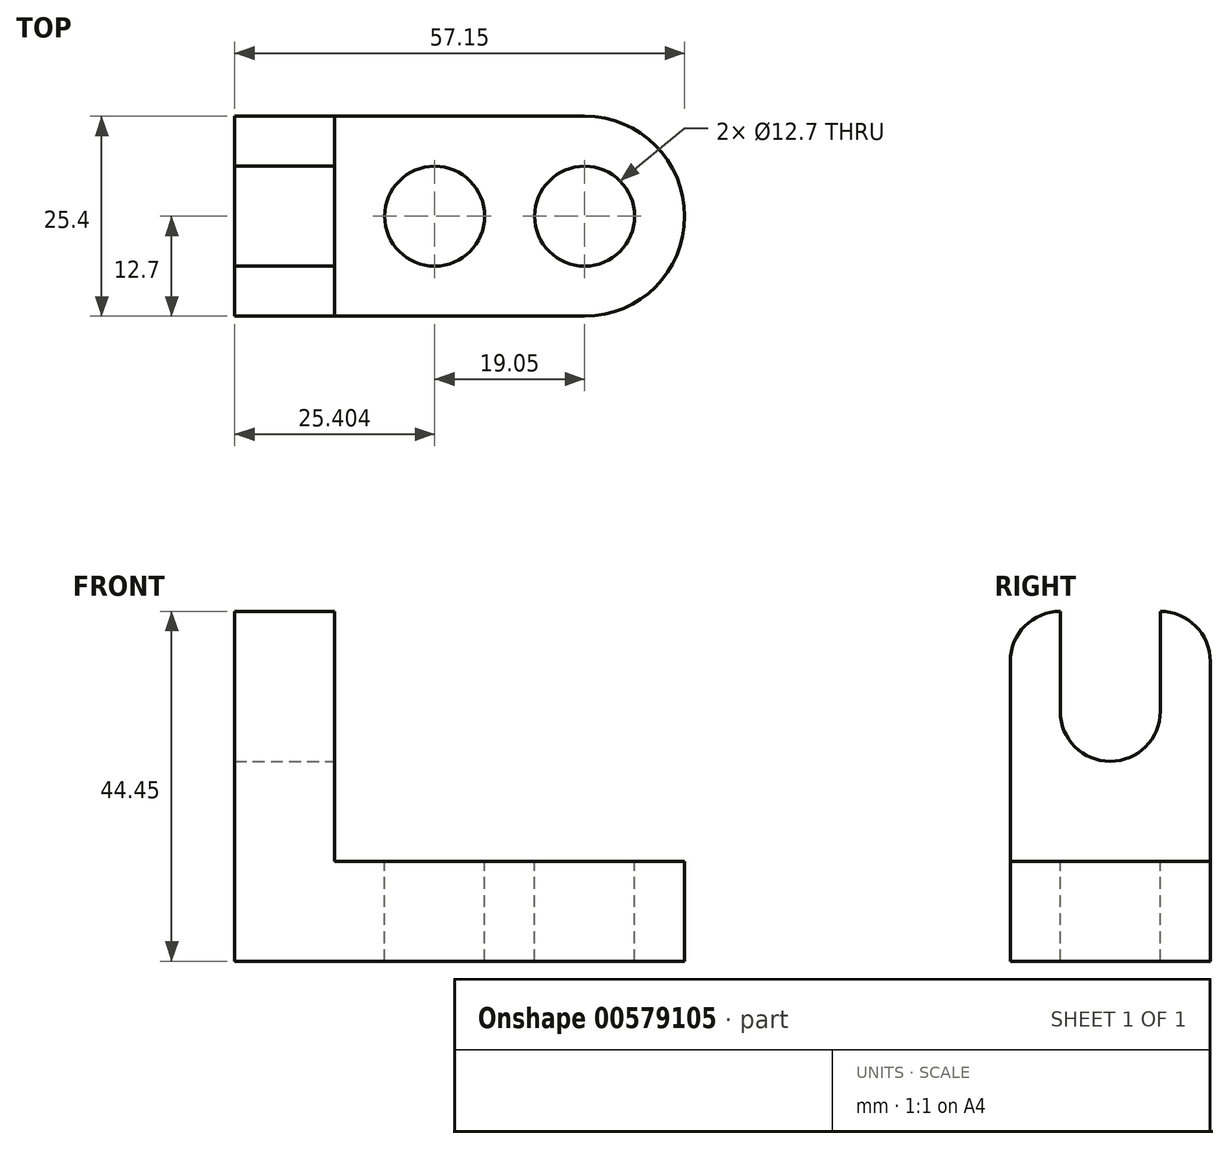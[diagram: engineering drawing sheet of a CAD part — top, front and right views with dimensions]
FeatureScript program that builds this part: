
annotation { "Feature Type Name" : "Feature", "Feature Type Description" : "" }
export const myFeature = defineFeature(function(context is Context, id is Id, definition is map)
    precondition{}
    {
        {
            var Q0;
            Q0=qCreatedBy(makeId("Front.planeOp"),FACE);
            var sketch = newSketch(context, id + "F0", { "sketchPlane" : qUnion([Q0])});
            skLineSegment(sketch, "E0", {"start": v(-64.2, 60.77) * mm, "end": v(-64.2, 16.32) * mm});
            skLineSegment(sketch, "E1", {"start": v(-64.2, 16.32) * mm, "end": v(-7.05, 16.32) * mm});
            skLineSegment(sketch, "E2", {"start": v(-7.05, 16.32) * mm, "end": v(-7.05, 29.02) * mm});
            skLineSegment(sketch, "E3", {"start": v(-7.05, 29.02) * mm, "end": v(-51.5, 29.02) * mm});
            skLineSegment(sketch, "E4", {"start": v(-51.5, 29.02) * mm, "end": v(-51.5, 60.77) * mm});
            skLineSegment(sketch, "E5", {"start": v(-51.5, 60.77) * mm, "end": v(-64.2, 60.77) * mm});
            skSolve(sketch);
        }
        {
            var Q0;
            Q0=makeQuery(id+"F0.imprint","IMPRINT",FACE,{"disambiguationData":[TD([[makeQuery(id+"F0.imprint","IMPRINT",EDGE,{"derivedFrom":sQuery(id+"F0.wireOp",EDGE,"E0")}),1.0]])]});
            extrude(context, id + "F1", {"entities" : qUnion([Q0]), "depth" : 25.4 * mm, "offsetDistance" : 25.4 * mm});
        }
        {
            var Q0;
            Q0=makeQuery(id+"F1.opExtrude","SWEPT_FACE",FACE,{"disambiguationData":[OSD([sQuery(id+"F0.wireOp",EDGE,"E3")])]});
            var sketch = newSketch(context, id + "F2", { "sketchPlane" : qUnion([Q0])});
            skCircle(sketch, "E6", {"center": v(-38.8, -12.7) * mm, "radius": 6.35 * mm});
            skCircle(sketch, "E7", {"center": v(-19.75, -12.7) * mm, "radius": 6.35 * mm});
            skSolve(sketch);
        }
        {
            var Q0;
            Q0=makeQuery(id+"F2.imprint","IMPRINT",FACE,{"disambiguationData":[TD([[makeQuery(id+"F2.imprint","IMPRINT",EDGE,{"derivedFrom":sQuery(id+"F2.wireOp",EDGE,"E6")}),1.0]])]});
            var Q1;
            Q1=makeQuery(id+"F2.imprint","IMPRINT",FACE,{"disambiguationData":[TD([[makeQuery(id+"F2.imprint","IMPRINT",EDGE,{"derivedFrom":sQuery(id+"F2.wireOp",EDGE,"E7")}),1.0]])]});
            extrude(context, id + "F3", {"entities" : qUnion([Q0, Q1]), "operationType" : NewBodyOperationType.REMOVE, "oppositeDirection" : true, "depth" : 25.4 * mm, "offsetDistance" : 25.4 * mm});
        }
        {
            var Q0;
            Q0=makeQuery(id+"F1.opExtrude","SWEPT_FACE",FACE,{"disambiguationData":[OSD([sQuery(id+"F0.wireOp",EDGE,"E4")])]});
            var sketch = newSketch(context, id + "F4", { "sketchPlane" : qUnion([Q0])});
            skCircle(sketch, "E8", {"center": v(-12.7, 48.07) * mm, "radius": 6.35 * mm});
            skLineSegment(sketch, "E9", {"start": v(-19.05, 48.07) * mm, "end": v(-19.05, 60.77) * mm});
            skLineSegment(sketch, "E10", {"start": v(-6.35, 48.07) * mm, "end": v(-6.35, 60.77) * mm});
            skSolve(sketch);
        }
        {
            var Q0;
            {var subQ0=sQuery(id+"F4.wireOp",EDGE,"E9");Q0=makeQuery(id+"F4.imprint","IMPRINT",FACE,{"disambiguationData":[TD([[makeQuery(id+"F4.imprint","IMPRINT",EDGE,{"derivedFrom":subQ0}),-1.0]])]});}
            var Q1;
            {var subQ0=sQuery(id+"F4.wireOp",EDGE,"E8");var subQ1=makeQuery(id+"F4.imprint","INTERSECT",VERTEX,{"derivedFrom":[subQ0,sQuery(id+"F4.wireOp",EDGE,"E9")]});Q1=makeQuery(id+"F4.imprint","IMPRINT",FACE,{"disambiguationData":[TD([[makeQuery(id+"F4.imprint","IMPRINT",EDGE,{"disambiguationData":[TD([[subQ1,1.0]])],"derivedFrom":subQ0}),1.0]])]});}
            extrude(context, id + "F5", {"entities" : qUnion([Q0, Q1]), "operationType" : NewBodyOperationType.REMOVE, "endBound" : BoundingType.THROUGH_ALL, "oppositeDirection" : true, "depth" : 25.4 * mm, "offsetDistance" : 25.4 * mm});
        }
        {
            var Q0;
            Q0=makeQuery(id+"F1.opExtrude","SWEPT_FACE",FACE,{"disambiguationData":[OSD([sQuery(id+"F0.wireOp",EDGE,"E4")])]});
            var sketch = newSketch(context, id + "F6", { "sketchPlane" : qUnion([Q0])});
            skCircle(sketch, "E11", {"center": v(-19.05, 54.42) * mm, "radius": 6.35 * mm});
            skCircle(sketch, "E12", {"center": v(-6.35, 54.42) * mm, "radius": 6.35 * mm});
            skSolve(sketch);
        }
        {
            var Q0;
            {var subQ1=sQuery(id+"F0.wireOp",EDGE,"E5");var subQ2=sQuery(id+"F0.wireOp",EDGE,"E4");var subQ3=sQuery(id+"F4.wireOp",EDGE,"E9");var subQ4=makeQuery(id+"F5.boolean.opBoolean","SPLIT",EDGE,{"disambiguationData":[TD([makeQuery(id+"F5.opExtrude","SWEPT_FACE",FACE,{"disambiguationData":[OSD([subQ3])]})])],"derivedFrom":makeQuery(id+"F1.opExtrude","SWEPT_EDGE",EDGE,{"disambiguationData":[OSD([subQ2,subQ1])]})});Q0=makeQuery(id+"F6.imprint","IMPRINT",FACE,{"disambiguationData":[TD([[makeQuery(id+"F6.imprint","IMPRINT",EDGE,{"derivedFrom":subQ4}),-1.0]])]});}
            var Q1;
            {var subQ1=sQuery(id+"F0.wireOp",EDGE,"E5");var subQ2=sQuery(id+"F0.wireOp",EDGE,"E4");var subQ3=sQuery(id+"F4.wireOp",EDGE,"E10");var subQ4=makeQuery(id+"F5.boolean.opBoolean","SPLIT",EDGE,{"disambiguationData":[TD([makeQuery(id+"F5.opExtrude","SWEPT_FACE",FACE,{"disambiguationData":[OSD([subQ3])]})])],"derivedFrom":makeQuery(id+"F1.opExtrude","SWEPT_EDGE",EDGE,{"disambiguationData":[OSD([subQ2,subQ1])]})});Q1=makeQuery(id+"F6.imprint","IMPRINT",FACE,{"disambiguationData":[TD([[makeQuery(id+"F6.imprint","IMPRINT",EDGE,{"derivedFrom":subQ4}),-1.0]])]});}
            extrude(context, id + "F7", {"entities" : qUnion([Q0, Q1]), "operationType" : NewBodyOperationType.REMOVE, "oppositeDirection" : true, "depth" : 25.4 * mm, "offsetDistance" : 25.4 * mm});
        }
        {
            var Q0;
            Q0=makeQuery(id+"F1.opExtrude","SWEPT_FACE",FACE,{"disambiguationData":[OSD([sQuery(id+"F0.wireOp",EDGE,"E3")])]});
            var sketch = newSketch(context, id + "F8", { "sketchPlane" : qUnion([Q0])});
            skCircle(sketch, "E13", {"center": v(-19.75, -12.7) * mm, "radius": 12.7 * mm});
            skSolve(sketch);
        }
        {
            var Q0;
            {var subQ0=sQuery(id+"F8.wireOp",EDGE,"E13");var subQ1=sQuery(id+"F0.wireOp",EDGE,"E3");var subQ2=makeQuery(id+"F1.opExtrude","CAP_EDGE",EDGE,{"disambiguationData":[OSD([subQ1])],"isStart":true});var subQ3=makeQuery(id+"F8.imprint","INTERSECT",VERTEX,{"derivedFrom":[subQ2,subQ0]});Q0=makeQuery(id+"F8.imprint","IMPRINT",FACE,{"disambiguationData":[TD([[makeQuery(id+"F8.imprint","IMPRINT",EDGE,{"disambiguationData":[TD([[subQ3,1.0]])],"derivedFrom":subQ0}),-1.0]])]});}
            var Q1;
            {var subQ0=sQuery(id+"F8.wireOp",EDGE,"E13");var subQ1=sQuery(id+"F0.wireOp",EDGE,"E3");var subQ4=makeQuery(id+"F1.opExtrude","CAP_EDGE",EDGE,{"disambiguationData":[OSD([subQ1])],"isStart":false});var subQ5=makeQuery(id+"F8.imprint","INTERSECT",VERTEX,{"derivedFrom":[subQ4,subQ0]});Q1=makeQuery(id+"F8.imprint","IMPRINT",FACE,{"disambiguationData":[TD([[makeQuery(id+"F8.imprint","IMPRINT",EDGE,{"disambiguationData":[TD([[subQ5,-1.0]])],"derivedFrom":subQ0}),-1.0]])]});}
            extrude(context, id + "F9", {"entities" : qUnion([Q0, Q1]), "operationType" : NewBodyOperationType.REMOVE, "oppositeDirection" : true, "depth" : 25.4 * mm, "offsetDistance" : 25.4 * mm});
        }
    });
